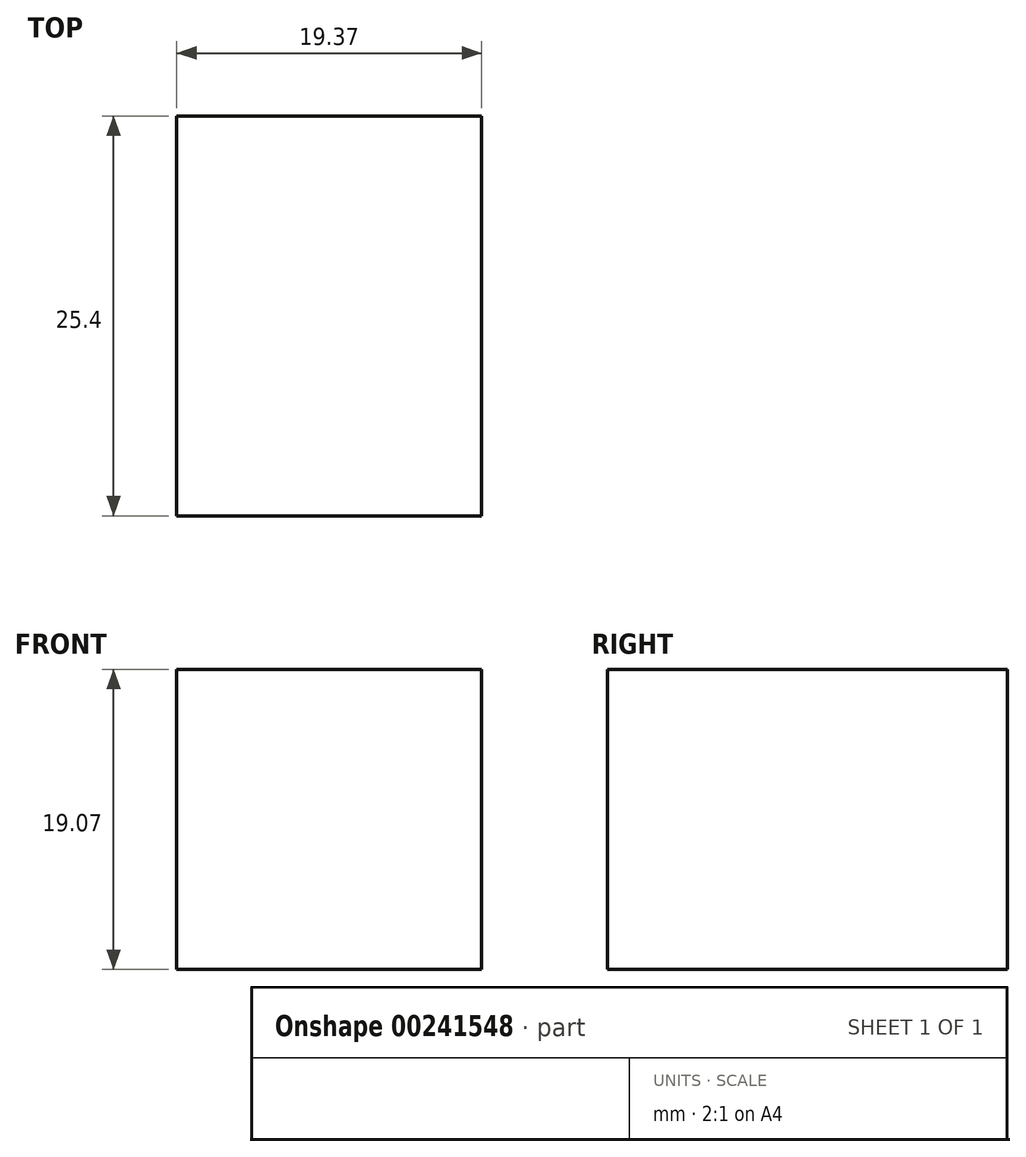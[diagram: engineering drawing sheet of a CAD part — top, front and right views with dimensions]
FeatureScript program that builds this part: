
annotation { "Feature Type Name" : "Feature", "Feature Type Description" : "" }
export const myFeature = defineFeature(function(context is Context, id is Id, definition is map)
    precondition{}
    {
        {
            var Q0;
            Q0=qCreatedBy(makeId("Front.planeOp"),FACE);
            var sketch = newSketch(context, id + "F0", { "sketchPlane" : qUnion([Q0])});
            skLineSegment(sketch, "E0", {"start": v(-35.35, 19.03) * mm, "end": v(-35.35, -14.64) * mm});
            skLineSegment(sketch, "E1", {"start": v(-35.35, -14.64) * mm, "end": v(-31.07, -25.08) * mm});
            skLineSegment(sketch, "E2", {"start": v(-31.07, -25.08) * mm, "end": v(18.93, -25.08) * mm});
            skLineSegment(sketch, "E3", {"start": v(18.93, -25.08) * mm, "end": v(18.93, 30.29) * mm});
            skLineSegment(sketch, "E4", {"start": v(18.93, 30.29) * mm, "end": v(31.45, 30.29) * mm});
            skLineSegment(sketch, "E5", {"start": v(31.45, 30.29) * mm, "end": v(23.16, 50.34) * mm});
            skLineSegment(sketch, "E6", {"start": v(23.16, 50.34) * mm, "end": v(7.2, 43.74) * mm});
            skLineSegment(sketch, "E7", {"start": v(7.2, 43.74) * mm, "end": v(-23.21, 43.74) * mm});
            skLineSegment(sketch, "E8", {"start": v(-23.21, 43.74) * mm, "end": v(-37.22, 43.74) * mm});
            skLineSegment(sketch, "E9", {"start": v(-37.22, 43.74) * mm, "end": v(-34.82, 15.82) * mm});
            skLineSegment(sketch, "E10", {"start": v(-34.82, 15.82) * mm, "end": v(-34.82, 15.82) * mm});
            skLineSegment(sketch, "E11", {"start": v(-35.35, 19.03) * mm, "end": v(-35.08, 18.9) * mm, "construction": true});
            skSolve(sketch);
        }
        {
            var Q0;
            Q0 = qSketchRegion(id + "F0", true);
            var Q1;
            Q1 = qBodyType(qCreatedBy(id + "F0" ,EDGE), BodyType.WIRE);
            extrude(context, id + "F1", {"entities" : qUnion([Q0]), "bodyType" : ToolBodyType.SURFACE, "operationType" : NewBodyOperationType.ADD, "surfaceEntities" : qUnion([Q1]), "depth" : 10 * mm});
        }
        {
            var Q0;
            Q0=qCreatedBy(makeId("Front.planeOp"),FACE);
            var sketch = newSketch(context, id + "F2", { "sketchPlane" : qUnion([Q0])});
            skLineSegment(sketch, "E12.bottom", {"start": v(-19.37, 23.4) * mm, "end": v(0, 23.4) * mm});
            skLineSegment(sketch, "E12.top", {"start": v(-19.37, 4.32) * mm, "end": v(0, 4.32) * mm});
            skLineSegment(sketch, "E12.left", {"start": v(-19.37, 23.4) * mm, "end": v(-19.37, 4.32) * mm});
            skLineSegment(sketch, "E12.right", {"start": v(0, 23.4) * mm, "end": v(0, 4.32) * mm});
            skSolve(sketch);
        }
        {
            var Q0;
            Q0 = qSketchRegion(id + "F2", true);
            extrude(context, id + "F3", {"entities" : qUnion([Q0]), "depth" : 25.4 * mm});
        }
    });
